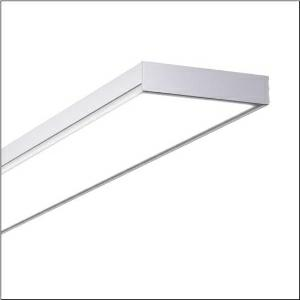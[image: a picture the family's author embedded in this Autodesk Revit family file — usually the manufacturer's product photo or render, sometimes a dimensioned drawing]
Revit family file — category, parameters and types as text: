
# Revit family: apollon_r__31_surface_51mp26wd2441e_9924
name_source: partatom
category: Lighting Fixtures
units: mm (PartAtom-declared; Revit-internal decimal feet)

## family parameters
Cut with Voids When Loaded = No
Host = Face
Light Source = No
Part Type = Normal
Room Calculation Point = No
Round Connector Dimension = Use Diameter
Shared = No

## types (1)
- Apollon® 31 Surface (1 x LED, 4600 lm, 33 W, 4000K)
    Apparent Load = 33 VA
    CIE Flux Codes = 61 87 97 97 100
    Color Rendering = 80
    Color Temperature = 4000K
    Default Elevation = 1800 mm
    Description = Apollon® 31 Surface, office luminaire, primary optical cover: micro prismatic cover, of PMMA, light emission: direct distribution, primary light characteristic: symmetric, installation type: surface-mounted, LED, rated luminous flux: 4.600lm, luminous efficacy: 139lm/W, light colour: 840, colour temperature: 4000K, control gear: DALI 2, with terminal, 5-pole, mains connection: 220..240V, AC, 50/60Hz, rated input power: 33W, housing, of sheet steel, coil coated, metallic grey (RAL 9006), length: 1.545mm, width: 200mm, height: 44mm, protection rating (complete): IP20, insulation class (complete): insulation class II (safety insulation), certification: CE, impact resistance: IK02, permissible operating ambient temperature: -20..+40°C, standard: EN 60598-2-22, packaging unit: 1 piece
    Height = 44 mm
    Lamp = 1 x LED
    Lamp Light Flux = 4600 lm
    Lamp Power = 33 W
    Lamp count = 1
    Length = 1545 mm
    Luminous efficacy = 139 lm/W
    Manufacturer = Siteco
    ModVariant = No
    Model = 51MP26WD2441E
    Mounting Place = Ceiling
    Mounting Type = Surface mounted
    Number of Poles = 1
    OnlyDefault = Yes
    Power Factor = 1
    Product Name = Apollon® 31 Surface
    Product group = office luminaire | ceiling mounted
    ProductGroupID = 302
    Protection Class = Protection class II
    Protection Degree = IP 20
    RLX_Detail_Level = 1
    RLX_Emergency_Light_Flux = 0 lm
    RLX_Emergency_Type = 0
    RLX_Emergency_Type_DB = No
    RlxData = <blob elided: 24093 chars, md5=389c2a66>
    Socket = socket
    Standby Power = 0 W
    System Light Flux = 4600 lm
    System Power = 33 W
    Type Comments = Product without accessories
    Type Image = l_1313654.jpg
    URL = http://relux.com
    VarID = ---
    Voltage = 0 V
    Weight = 0.00 kg
    Width = 200 mm  [stored 0.656168 ft]

note: [stored X ft] marks values corroborated as IEEE doubles in the binary element streams (Revit-internal decimal feet)

## geometry (parser evidence)
native form markers: Blend x4, Sweep x9
no freeform markers — native parametric forms only
